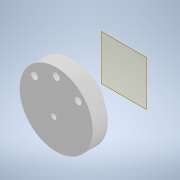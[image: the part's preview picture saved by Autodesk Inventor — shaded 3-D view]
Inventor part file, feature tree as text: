
AUTODESK INVENTOR PART (.ipt)
format: ipt  version: 2022 (Build 260153000, 153)  size: 182,784 bytes
history: native  units: mm
features: extrude x8, sketch x8, other x5, reference x4, chamfer x1, mirror x1, projected_geometry x1
ambient origin geometry x8: Origin, YZ Plane, XZ Plane, XY Plane, X Axis, Y Axis, Z Axis, Center Point
bodies: Body1 (feature_tree)
feature tree (28):
  other  "Твердое тело1"
  extrude  "Выдавливание1"  Depth=45.0mm
  extrude  "Выдавливание2"  Depth=9.295mm TaperAngle=0.0deg
  extrude  "Выдавливание3"  Depth=25.2mm
  chamfer  "Фаска1"  Distance=7.8mm
  extrude  "Выдавливание4"  Depth=2.0mm
  extrude  "Выдавливание5"  Depth=1.0mm TaperAngle=0.0deg
  extrude  "Выдавливание6"  Depth=0.5mm TaperAngle=45.0deg
  extrude  "Выдавливание7"  Depth=4.0mm
  other  "РабПлоскость1"
  mirror  "Зеркальное отражение1"
  extrude  "Выдавливание8"  Depth=0.5mm
  sketch  "Эскиз1"
  sketch  "Эскиз2"
  sketch  "Эскиз3"
  projected_geometry  "Спроецированная петля1"
  sketch  "Эскиз4"
  sketch  "Эскиз5"
  reference  "Ссылка1"
  reference  "Ссылка2"
  reference  "Ссылка3"
  sketch  "Эскиз6"
  reference  "Ссылка4"
  sketch  "Эскиз7"
  sketch  "Эскиз8"
  other  "<userpath>\Documents\Git\MZCAT_2024\MZCAT.iam"
  other  "MZCAT.iam"
  other  "base plate:2"
